# Revit family: REVIT-PVX_1UX0
name_source: partatom
category: Mechanical Equipment
revit_build: Autodesk Revit 2017 (Build: 20190507_1515(x64)
units: mm (PartAtom-declared; Revit-internal decimal feet)

## family parameters
Always vertical = Yes
Cut with Voids When Loaded = No
Part Type = Normal
Room Calculation Point = No
Round Connector Dimension = Use Radius
Shared = No
Work Plane-Based = No

## types (3) — shared parameters
Air Inlet Location = 22 27/32"
Air Inlet Radius = 3"
Apparent Load = 1800 VA
Assembly Code = D3020100
Building Return Extension = 22 1/2"
Building Return Height = 44"
Building Return NPT = 2"
Building Return Radius = 1"
Burner Conn Height = 71 5/8"
Burner Height = 18"
Burner Housing Extension = 37 7/16"
Burner Housing Height = 17"
Burner Housing Outlet Extension = 29 13/16"
Burner Housing to Left = 8 11/16"
Burner Housing to Right = 2 3/16"
Burner Width = 6"
Cold Inlet Extension = 22 1/2"
Cold Inlet Height = 12 3/4"
Cold Inlet NPT = 2"
Cold Inlet Radius = 1"
Combustion Air Connection = 6"
Combustion Air Connection X = 5 7/16"
Combustion Air Connection Y = 36"
Combustion Air Inlet Radius = 3"
Condensate Connection = 3/4"
Condensate Drain Extension = 12"
Condensate Extension = 28"
Condensate Location = 4"
Condensate Radius = 3/8"
Control Panel Extension = 28 1/2"
Current = 11 A
Description = PWER VTX™ Condensing Water Heater
Disclaimer = This rendering is for building modeling purposes only. Submittal/catalog is still the contract document. PVI reserves the right to change design and specification without notice.
Drain Angle = 45.00°
Drain Extension = 25 3/8"
Drain Height = 12 3/4"
Drain NPT = 1"
Drain Radius = 1/2"
Enclosure Angle = 45.00°
Enclosure Height = 38 5/16"
Enclosure Width = 12"
Front Skid = 22 1/2"
Gas Inlet NPT = 1 1/2"
Gas Inlet Radius = 3/4"
Gas Train Extension = 15 7/16"
Gas Train Location = 10 7/16"
Gas Train To Front = 31"
Height to Enclosure = 25"
Height to Pump = 58"
Hot Outlet Extension = 22 1/2"
Hot Outlet Height = 67 3/4"
Hot Outlet NPT = 2"
Hot Outlet Radius = 1"
Manufacturer = PVI Industries, LLC
Model = This message indicated family is not loaded properly. Please load again.
Pump Angle = 45.00°
Pump Extension = 25 7/8"
Relief 1 Angle = 40.00°
Relief 2 Angle = 60.00°
Relief Angle = 90.00°
Relief Extension = 25 1/2"
Relief Height = 65"
Relief NPT = 3/4"
Relief Radius = 3/8"
Skid Length = 45"
Skid Spacing = 20 5/8"
URL = www.pvi.com
Unit Height = 76 5/8"
Unit Radius = 21 1/2"
Vent Angle = 0.00°
Vent Connection = 6 5/8"
Vent Extension = 24 7/8"
Vent Height = 7"
Vent Radius = 3 5/16"

## per-type parameters (varying)
| type | Gas Train Height | Height to Combustion Air Connection | Input | Recovery Rate 40F to 140F (gph) | Weight |
| 50 L 225A-PVX | 11 3/8" | 75 1/4" | 500000 Btu/h | 582 | 1520 |
| 75 L 225A-PVX | 14 7/8" | 81 3/4" | 750000 Btu/h | 873 | 1610 |
| 100 L 225A-PVX | 14 7/8" | 81 3/4" | 999000 Btu/h | 1163 | 1700 |

## geometry (parser evidence)
native form markers: Sweep x2
no freeform markers — native parametric forms only
